FCSTD DOCUMENT  (FreeCAD 1.0R39319 (Git))
Label: Week2Sketch2
License: All rights reserved
LicenseURL: https://en.wikipedia.org/wiki/All_rights_reserved
objects: Sketcher::SketchObject×1, PartDesign::Body×1, Spreadsheet::Sheet×1
note: 3 computed .brp shape members not serialized (recipe doc carries the construction recipe); baked Part::Feature solids carry a one-line shape summary decoded from their .brp

FEATURE [Sketcher::SketchObject] Sketch
  ArcFitTolerance = 1e-06
  AttachmentSupport = -> [XY_Plane]
  FullyConstrained = true
  MakeInternals = false
  MapMode = 5
  expr: Constraints[109] = <<Spreadsheet>>.gear_tooth_rad
  expr: Constraints[34] = <<Spreadsheet>>.botleft_xdist
  expr: Constraints[35] = <<Spreadsheet>>.botright_step_ydist
  expr: Constraints[36] = <<Spreadsheet>>.botmid_xdist
  expr: Constraints[37] = <<Spreadsheet>>.botmid_xdist
  expr: Constraints[38] = <<Spreadsheet>>.midstep_ydist
  expr: Constraints[39] = <<Spreadsheet>>.portr_xdist
  expr: Constraints[40] = <<Spreadsheet>>.portr_edge_xdist
  expr: Constraints[44] = <<Spreadsheet>>.left_portr_ydist
  expr: Constraints[56] = <<Spreadsheet>>.edgecut_xdist
  expr: Constraints[58] = <<Spreadsheet>>.edgecut_ydist
  expr: Constraints[5] = <<Spreadsheet>>.height
  expr: Constraints[77] = <<Spreadsheet>>.inner_dip_len
  expr: Constraints[78] = <<Spreadsheet>>.inner_dip_depth
  expr: Constraints[81] = <<Spreadsheet>>.topright_xdist
  expr: Constraints[82] = <<Spreadsheet>>.topmid_xdist
  expr: Constraints[84] = <<Spreadsheet>>.gear_inner_rad * 2
  expr: Constraints[85] = <<Spreadsheet>>.gear_outer_rad * 2
  expr: Constraints[95] = <<Spreadsheet>>.slant_len
  expr: Constraints[96] = <<Spreadsheet>>.fillet_rad
  sketch-geometry (57):
    g0: LineSegment StartX=-59 StartY=66.9264 StartZ=0 EndX=-59 EndY=37 EndZ=0
    g1: LineSegment StartX=-17 StartY=0 StartZ=0 EndX=-5 EndY=0 EndZ=0
    g2: LineSegment StartX=0 StartY=5 StartZ=0 EndX=0 EndY=57 EndZ=0
    g3: LineSegment StartX=0 StartY=75 StartZ=0 EndX=-18 EndY=75 EndZ=0
    g4: GeomPoint [constr] X=-59 Y=75 Z=0
    g5: ArcOfCircle CenterX=-5 CenterY=5 CenterZ=0 NormalX=0 NormalY=0 NormalZ=1 AngleXU=0 Radius=5 StartAngle=4.71239 EndAngle=6.28319
    g6: GeomPoint [constr] X=0 Y=0 Z=0
    g7: LineSegment StartX=-17 StartY=0 StartZ=0 EndX=-17 EndY=15 EndZ=0
    g8: LineSegment StartX=-17 StartY=15 StartZ=0 EndX=-38 EndY=15 EndZ=0
    g9: LineSegment StartX=-38 StartY=15 StartZ=0 EndX=-38 EndY=37 EndZ=0
    g10: LineSegment StartX=-38 StartY=37 StartZ=0 EndX=-42 EndY=37 EndZ=0
    g11: LineSegment StartX=-42 StartY=37 StartZ=0 EndX=-42 EndY=27 EndZ=0
    g12: LineSegment StartX=-42 StartY=27 StartZ=0 EndX=-46 EndY=27 EndZ=0
    g13: LineSegment StartX=-46 StartY=27 StartZ=0 EndX=-46 EndY=31 EndZ=0
    g14: LineSegment StartX=-46 StartY=31 StartZ=0 EndX=-50 EndY=31 EndZ=0
    g15: LineSegment StartX=-50 StartY=31 StartZ=0 EndX=-50 EndY=27 EndZ=0
    g16: LineSegment StartX=-50 StartY=27 StartZ=0 EndX=-54 EndY=27 EndZ=0
    g17: LineSegment StartX=-54 StartY=27 StartZ=0 EndX=-54 EndY=37 EndZ=0
    g18: LineSegment StartX=-54 StartY=37 StartZ=0 EndX=-59 EndY=37 EndZ=0
    g19: LineSegment StartX=0 StartY=61 StartZ=0 EndX=-4 EndY=61 EndZ=0
    g20: LineSegment StartX=-4 StartY=61 StartZ=0 EndX=-4 EndY=57 EndZ=0
    g21: LineSegment StartX=-4 StartY=57 StartZ=0 EndX=0 EndY=57 EndZ=0
    g22: LineSegment StartX=0 StartY=61 StartZ=0 EndX=0 EndY=75 EndZ=0
    g23: LineSegment StartX=-40 StartY=72.8297 StartZ=0 EndX=-40 EndY=55.1267 EndZ=0
    g24: LineSegment StartX=-40 StartY=55.1267 StartZ=0 EndX=-33 EndY=55.1267 EndZ=0
    g25: LineSegment StartX=-33 StartY=55.1267 StartZ=0 EndX=-33 EndY=51.1267 EndZ=0
    g26: LineSegment StartX=-33 StartY=51.1267 StartZ=0 EndX=-25 EndY=51.1267 EndZ=0
    g27: LineSegment StartX=-25 StartY=51.1267 StartZ=0 EndX=-25 EndY=55.1267 EndZ=0
    g28: LineSegment StartX=-25 StartY=55.1267 StartZ=0 EndX=-18 EndY=55.1267 EndZ=0
    g29: LineSegment StartX=-18 StartY=55.1267 StartZ=0 EndX=-18 EndY=75 EndZ=0
    g30: ArcOfCircle CenterX=-17 CenterY=37 CenterZ=0 NormalX=0 NormalY=0 NormalZ=1 AngleXU=0 Radius=8.5 StartAngle=5.61635 EndAngle=5.70154
    g31: Circle [constr] CenterX=-17 CenterY=37 CenterZ=0 NormalX=0 NormalY=0 NormalZ=1 AngleXU=0 Radius=6.4
    g32: ArcOfCircle CenterX=-54 CenterY=66.9264 CenterZ=0 NormalX=0 NormalY=0 NormalZ=1 AngleXU=0 Radius=5 StartAngle=1.76626 EndAngle=3.14159
    g33: LineSegment StartX=-54.9711 StartY=71.8311 StartZ=0 EndX=-42.629 EndY=74.2748 EndZ=0
    g34: LineSegment StartX=-42.629 StartY=74.2748 StartZ=0 EndX=-40 EndY=72.8297 EndZ=0
    g35: LineSegment [constr] StartX=-17 StartY=45.5 StartZ=0 EndX=-17 EndY=28.5 EndZ=0
    g36: LineSegment [constr] StartX=-25.5 StartY=37 StartZ=0 EndX=-8.5 EndY=37 EndZ=0
    g37: GeomPoint [constr] X=-17 Y=30.6 Z=0
    g38: ArcOfCircle CenterX=-17 CenterY=28.5 CenterZ=0 NormalX=0 NormalY=0 NormalZ=1 AngleXU=0 Radius=2.2 StartAngle=0.129776 EndAngle=3.01182
    g39: ArcOfCircle CenterX=-17 CenterY=45.5 CenterZ=0 NormalX=0 NormalY=0 NormalZ=1 AngleXU=0 Radius=2.2 StartAngle=3.27137 EndAngle=6.15341
    g40: ArcOfCircle CenterX=-11.8939 CenterY=30.2046 CenterZ=0 NormalX=0 NormalY=0 NormalZ=1 AngleXU=0 Radius=2.2 StartAngle=0.77418 EndAngle=3.65622
    g41: ArcOfCircle CenterX=-8.93711 CenterY=34.3093 CenterZ=0 NormalX=0 NormalY=0 NormalZ=1 AngleXU=0 Radius=2.2 StartAngle=1.37848 EndAngle=4.26052
    g42: ArcOfCircle CenterX=-17 CenterY=37 CenterZ=0 NormalX=0 NormalY=0 NormalZ=1 AngleXU=0 Radius=8.5 StartAngle=6.22064 EndAngle=6.34573
    g43: ArcOfCircle CenterX=-17 CenterY=37 CenterZ=0 NormalX=0 NormalY=0 NormalZ=1 AngleXU=0 Radius=8.5 StartAngle=4.97194 EndAngle=5.09724
    g44: ArcOfCircle CenterX=-12.0018 CenterY=43.8752 CenterZ=0 NormalX=0 NormalY=0 NormalZ=1 AngleXU=0 Radius=2.2 StartAngle=2.64275 EndAngle=5.52479
    g45: ArcOfCircle CenterX=-8.93711 CenterY=39.6907 CenterZ=0 NormalX=0 NormalY=0 NormalZ=1 AngleXU=0 Radius=2.2 StartAngle=2.02267 EndAngle=4.90471
    g46: ArcOfCircle CenterX=-17 CenterY=37 CenterZ=0 NormalX=0 NormalY=0 NormalZ=1 AngleXU=0 Radius=8.5 StartAngle=1.20173 EndAngle=1.31124
    g47: ArcOfCircle CenterX=-17 CenterY=37 CenterZ=0 NormalX=0 NormalY=0 NormalZ=1 AngleXU=0 Radius=8.5 StartAngle=0.581645 EndAngle=0.68263
    g48: ArcOfCircle CenterX=-17 CenterY=37 CenterZ=0 NormalX=0 NormalY=0 NormalZ=1 AngleXU=0 Radius=8.5 StartAngle=1.83035 EndAngle=1.93986
    g49: ArcOfCircle CenterX=-21.9982 CenterY=43.8752 CenterZ=0 NormalX=0 NormalY=0 NormalZ=1 AngleXU=0 Radius=2.2 StartAngle=3.89998 EndAngle=6.78202
    g50: ArcOfCircle CenterX=-25.0629 CenterY=39.6907 CenterZ=0 NormalX=0 NormalY=0 NormalZ=1 AngleXU=0 Radius=2.2 StartAngle=4.52007 EndAngle=7.40211
    g51: ArcOfCircle CenterX=-25.0629 CenterY=34.3093 CenterZ=0 NormalX=0 NormalY=0 NormalZ=1 AngleXU=0 Radius=2.2 StartAngle=5.16426 EndAngle=8.0463
    g52: ArcOfCircle CenterX=-22.1061 CenterY=30.2046 CenterZ=0 NormalX=0 NormalY=0 NormalZ=1 AngleXU=0 Radius=2.2 StartAngle=5.76856 EndAngle=8.6506
    g53: ArcOfCircle CenterX=-17 CenterY=37 CenterZ=0 NormalX=0 NormalY=0 NormalZ=1 AngleXU=0 Radius=8.5 StartAngle=2.45896 EndAngle=2.55995
    g54: ArcOfCircle CenterX=-17 CenterY=37 CenterZ=0 NormalX=0 NormalY=0 NormalZ=1 AngleXU=0 Radius=8.5 StartAngle=3.07905 EndAngle=3.20413
    g55: ArcOfCircle CenterX=-17 CenterY=37 CenterZ=0 NormalX=0 NormalY=0 NormalZ=1 AngleXU=0 Radius=8.5 StartAngle=3.72324 EndAngle=3.80843
    g56: ArcOfCircle CenterX=-17 CenterY=37 CenterZ=0 NormalX=0 NormalY=0 NormalZ=1 AngleXU=0 Radius=8.5 StartAngle=4.32754 EndAngle=4.45284
  constraints (168):
    c: Coincident(g22,g3)
    c: Vertical(g0)
    c: Vertical(g2)
    c: Horizontal(g1)
    c: Horizontal(g3)
    c: DistanceY(g-1,g4) = 75
    c: PointOnObject(g4,g0)
    c: PointOnObject(g6,g1)
    c: PointOnObject(g6,g2)
    c: Tangent(g1,g5) = -1.5708
    c: Tangent(g2,g5) = -1.5708
    c: Vertical(g7)
    c: Coincident(g7,g8)
    c: Horizontal(g8)
    c: Coincident(g8,g9)
    c: Vertical(g9)
    c: Coincident(g9,g10)
    c: Horizontal(g10)
    c: Coincident(g10,g11)
    c: Vertical(g11)
    c: Coincident(g11,g12)
    c: Coincident(g12,g13)
    c: Vertical(g13)
    c: Coincident(g13,g14)
    c: Coincident(g14,g15)
    c: Vertical(g15)
    c: Coincident(g15,g16)
    c: Horizontal(g16)
    c: Coincident(g16,g17)
    c: Vertical(g17)
    c: Coincident(g17,g18)
    c: Horizontal(g18)
    c: Horizontal(g14)
    c: Horizontal(g12)
    c: Distance(g2,g7) = 17
    c: DistanceY(g7,g7) = 15
    c: DistanceX(g8,g8) = 21
    c: Distance(g0,g9) = 21
    c: DistanceY(g9,g9) = 22
    c: DistanceX(g10,g10) = 4
    c: DistanceX(g18,g18) = 5
    c: Equal(g16,g12)
    c: Equal(g15,g13)
    c: Equal(g17,g11)
    c: DistanceY(g17,g17) = 10
    c: DistanceX(g14,g14) = 4  'TEMP'
    c: DistanceY(g15,g15) = 4  'TEMPO'
    c: Coincident(g0,g18)
    c: Coincident(g1,g7)
    c: Coincident(g6,g-1)
    c: Coincident(g19,g20)
    c: Coincident(g20,g21)
    c: Horizontal(g19)
    c: Horizontal(g21)
    c: Vertical(g20)
    c: PointOnObject(g19,g22)
    c: DistanceY(g20,g20) = 4
    c: Equal(g20,g19)
    c: Distance(g-1,g21) = 57
    c: PointOnObject(g2,g21)
    c: PointOnObject(g22,g19)
    c: PointOnObject(g3,g-2)
    c: PointOnObject(g19,g-2)
    c: PointOnObject(g21,g2)
    c: Vertical(g23)
    c: Coincident(g23,g24)
    c: Horizontal(g24)
    c: Coincident(g24,g25)
    c: Vertical(g25)
    c: Coincident(g25,g26)
    c: Horizontal(g26)
    c: Coincident(g26,g27)
    c: Vertical(g27)
    c: Coincident(g27,g28)
    c: Horizontal(g28)
    c: Coincident(g28,g29)
    c: Vertical(g29)
    c: DistanceX(g26,g26) = 8
    c: DistanceY(g27,g27) = 4
    c: Equal(g25,g27)
    c: Equal(g24,g28)
    c: Distance(g22,g29) = 18
    c: Distance(g29,g23) = 22
    c: Coincident(g31,g30)
    c: Diameter(g31) = 12.8
    c: Diameter(g30) = 17
    c: Vertical(g30,g7)
    c: Horizontal(g9,g30)
    c: Block(g23)
    c: Coincident(g3,g29)
    c: Horizontal(g4,g3)
    c: Tangent(g0,g32) = -1.5708
    c: Coincident(g33,g34)
    c: Tangent(g32,g33) = 1.5708
    c: Equal(g5,g32)
    c: Distance(g34,g34) = 3
    c: Radius(g32) = 5
    c: Coincident(g23,g34)
    c: Block(g32)
    c: PointOnObject(g35,g43)
    c: Vertical(g35)
    c: PointOnObject(g30,g35)
    c: PointOnObject(g36,g54)
    c: PointOnObject(g36,g42)
    c: Horizontal(g36)
    c: PointOnObject(g30,g36)
    c: PointOnObject(g37,g35)
    c: PointOnObject(g37,g31)
    c: Coincident(g38,g35)
    c: Radius(g38) = 2.2
    c: Radius(g39) = 2.2
    c: Block(g39)
    c: PointOnObject(g40,g48)
    c: PointOnObject(g41,g30)
    c: PointOnObject(g41,g42)
    c: Equal(g38,g40)
    c: Equal(g40,g41)
    c: Coincident(g43,g40)
    c: Coincident(g30,g40)
    c: Coincident(g30,g41)
    c: PointOnObject(g42,g41)
    c: Coincident(g30,g42)
    c: Equal(g42,g43)
    c: Coincident(g56,g38)
    c: Coincident(g42,g43)
    c: Coincident(g43,g38)
    c: Equal(g44,g45)
    c: Equal(g42,g46)
    c: PointOnObject(g47,g44)
    c: PointOnObject(g46,g44)
    c: Coincident(g42,g46)
    c: Equal(g42,g47)
    c: PointOnObject(g42,g45)
    c: PointOnObject(g47,g45)
    c: Coincident(g42,g47)
    c: Equal(g43,g30)
    c: Equal(g46,g48)
    c: PointOnObject(g48,g39)
    c: Coincident(g46,g48)
    c: PointOnObject(g46,g39)
    c: Equal(g52,g51)
    c: Equal(g49,g50)
    c: Block(g44)
    c: Block(g45)
    c: Block(g40)
    c: Block(g41)
    c: Block(g52)
    c: Block(g51)
    c: Block(g50)
    c: Block(g49)
    c: Equal(g48,g53)
    c: PointOnObject(g48,g49)
    c: PointOnObject(g53,g49)
    c: Coincident(g48,g53)
    c: Equal(g53,g54)
    c: PointOnObject(g53,g50)
    c: PointOnObject(g54,g50)
    c: Coincident(g53,g54)
    c: Equal(g54,g55)
    c: PointOnObject(g54,g51)
    c: PointOnObject(g55,g51)
    c: Coincident(g54,g55)
    c: Equal(g55,g56)
    c: PointOnObject(g55,g52)
    c: PointOnObject(g56,g52)
    c: Coincident(g55,g56)
    c: Block(g46)
    c: Block(g35)
FEATURE [PartDesign::Body] Body
  AllowCompound = false
  Group = -> [Sketch]
  Origin = -> Origin
FEATURE [Spreadsheet::Sheet] Spreadsheet
  cells = A1='gear_inner_rad; B1(gear_inner_rad)=6.4; A2='gear_outer_rad; B2(gear_outer_rad)=8.5; A3='gear_tooth_rad; B3(gear_tooth_rad)=2.2; A4='fillet_rad; B4(fillet_rad)=5; A5='botright_step_ydist; B5(botright_step_ydist)=15; A6='midstep_ydist; B6(midstep_ydist)=22; A7='left_portr_ydist; B7(left_portr_ydist)=10; A8='portr_xdist; B8(portr_xdist)=4; A9='portr_edge_xdist; B9(portr_edge_xdist)=5; A10='botleft_xdist; B10(botleft_xdist)=17; A11='botmid_xdist; B11(botmid_xdist)=21; A12='topright_xdist; B12(topright_xdist)=18; A13='topmid_xdist; B13(topmid_xdist)=22; A14='edgecut_ydist; B14(edgecut_ydist)=57; A15='edgecut_xdist; B15(edgecut_xdist)=4; A16='height; B16(height)=75; A17='slant_len; B17(slant_len)=3; A18='inner_dip_len; B18(inner_dip_len)=8; A19='dip_length; B19(dip_length)=22; A20='inner_dip_depth; B20(inner_dip_depth)=4
